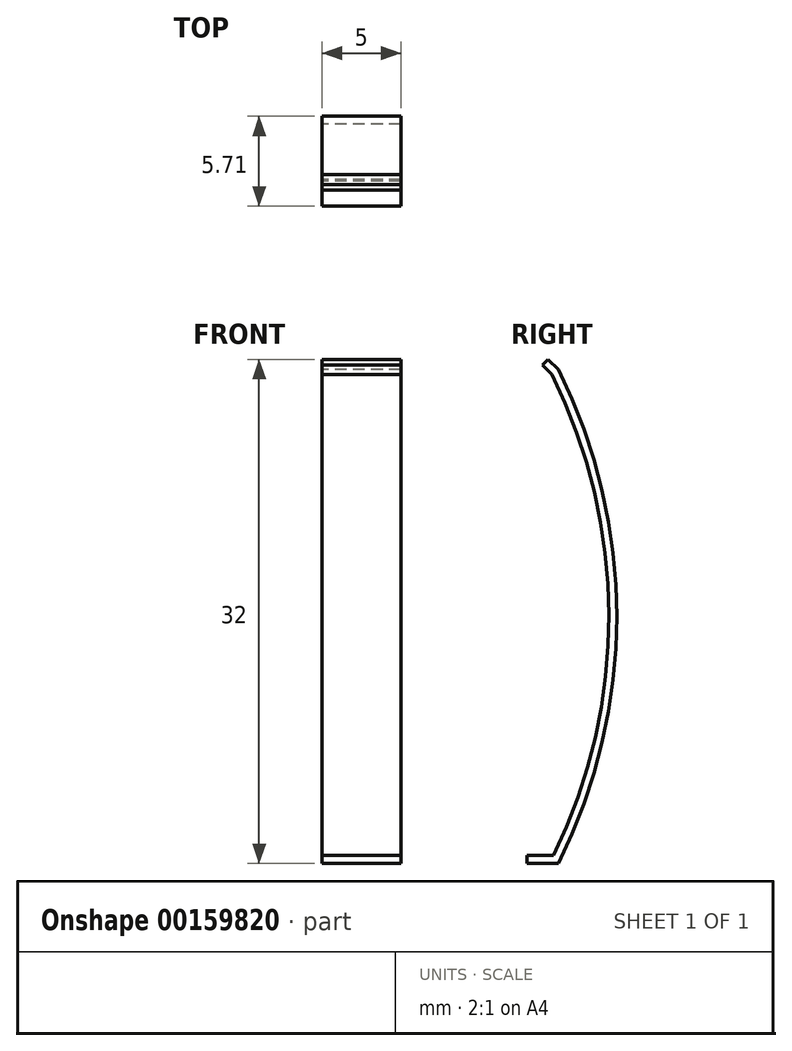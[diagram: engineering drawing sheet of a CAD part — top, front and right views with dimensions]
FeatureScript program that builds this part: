
annotation { "Feature Type Name" : "Feature", "Feature Type Description" : "" }
export const myFeature = defineFeature(function(context is Context, id is Id, definition is map)
    precondition{}
    {
        {
            var Q0;
            Q0=qCreatedBy(makeId("Right.planeOp"),FACE);
            var sketch = newSketch(context, id + "F0", { "sketchPlane" : qUnion([Q0])});
            skLineSegment(sketch, "E0", {"start": v(0, 0) * mm, "end": v(2, 0) * mm});
            skArc(sketch, "E1", {"start": v(2, 0) * mm, "mid": v(5.7, 15.68) * mm, "end": v(2, 31.35) * mm});
            skArc(sketch, "E2.1", {"start": v(1.69, 0.5) * mm, "mid": v(5.2, 15.8) * mm, "end": v(1.59, 31.06) * mm});
            skLineSegment(sketch, "E2.2", {"start": v(0, 0.5) * mm, "end": v(1.69, 0.5) * mm});
            skLineSegment(sketch, "E3", {"start": v(0, 0) * mm, "end": v(0, 0.5) * mm});
            skLineSegment(sketch, "E4", {"start": v(2, 31.35) * mm, "end": v(1.35, 32) * mm});
            skLineSegment(sketch, "E5", {"start": v(1.59, 31.06) * mm, "end": v(1, 31.65) * mm});
            skLineSegment(sketch, "E6", {"start": v(1.35, 32) * mm, "end": v(1, 31.65) * mm});
            skSolve(sketch);
        }
        {
            var Q0;
            Q0=qSketchRegion(id+"F0",true);
            extrude(context, id + "F1", {"entities" : qUnion([Q0]), "depth" : 5 * mm});
        }
    });
